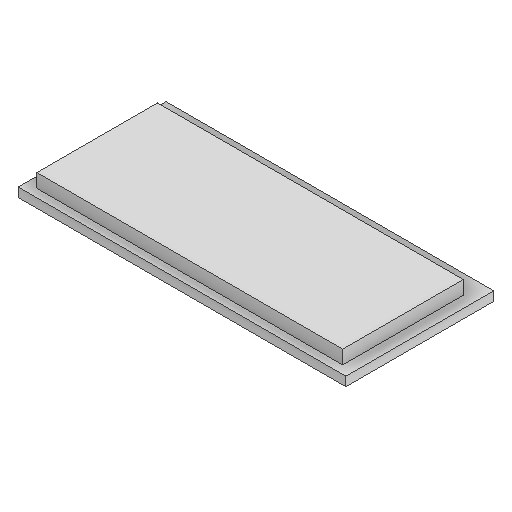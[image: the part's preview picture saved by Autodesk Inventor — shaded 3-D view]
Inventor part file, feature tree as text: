
AUTODESK INVENTOR PART (.ipt)
format: ipt  version: 2025.1 (Build 291241020, 241B)  size: 134,144 bytes
history: native  units: in
note: dims shown in document units (in); Inventor stores cm internally (conversion verified against a paired STEP export)
features: extrude x4, sketch x4
ambient origin geometry x8: Origin, YZ Plane, XZ Plane, XY Plane, X Axis, Y Axis, Z Axis, Center Point
bodies: Solid1 (feature_tree)
feature tree (8):
  extrude  "Extrusion1"  Depth=7.2in
  extrude  "Extrusion2"  Depth=0.23in
  extrude  "Extrusion3"  Depth=0.18in
  extrude  "Extrusion4"  Depth=0.3in TaperAngle=0.0deg
  sketch  "Sketch1"  dims[d0=3.25in d1=7.2in]
  sketch  "Sketch2"  dims[d2=0.2in d3=0.0in d4=0.23in]
  sketch  "Sketch3"  dims[d5=0.25in d6=0.18in]
  sketch  "Sketch4"  dims[d7=0.42in d8=0.3in d9=0.0in d10=1.26in d11=0.48in d12=1.0in d13=0.16in d14=0.25in d15=0.0in d16=0.86in d17=0.46in d18=0.5in d19=0.0in]
